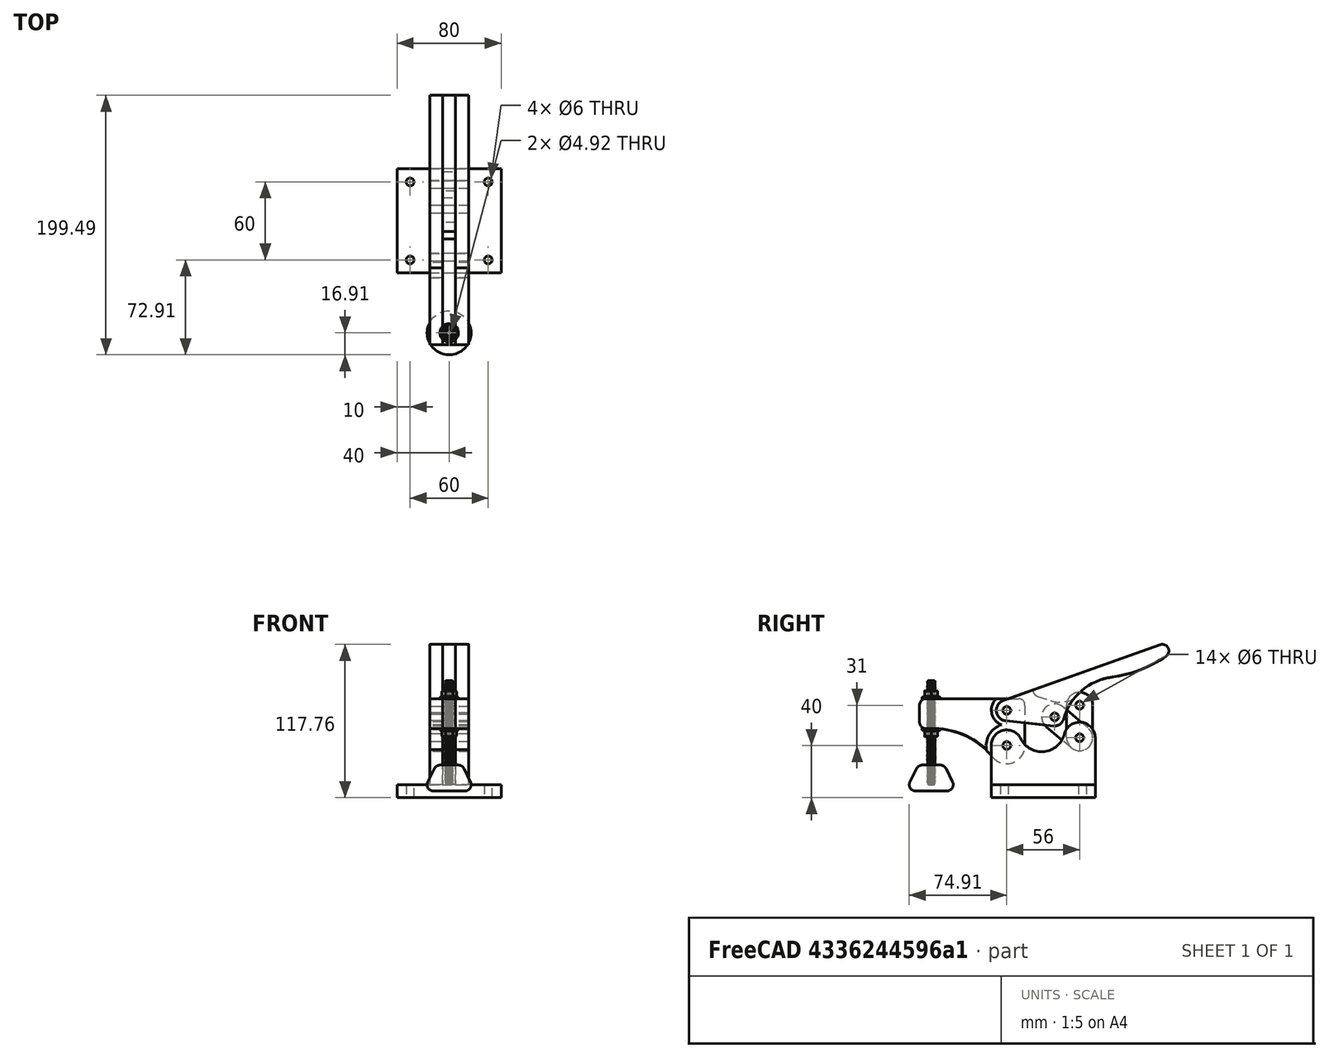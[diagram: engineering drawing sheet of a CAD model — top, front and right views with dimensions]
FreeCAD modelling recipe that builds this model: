
FCSTD DOCUMENT  (FreeCAD 0.19R23756 (Git))
Label: 207 - Tech Draw
License: Creative Commons Attribution-NonCommercial
LicenseURL: http://creativecommons.org/licenses/by-nc/4.0/
objects: TechDraw::DrawViewDimension×57, Part::FeaturePython×14, TechDraw::DrawProjGroupItem×8, TechDraw::DrawViewAnnotation×7, TechDraw::DrawProjGroup×6, Part::Cylinder×4, Part::Compound×4, TechDraw::DrawViewBalloon×4, Part::Cone×1, Part::Fillet×1, TechDraw::DrawSVGTemplate×1, TechDraw::DrawViewImage×1, TechDraw::DrawPage×1
note: 24 computed .brp shape members not serialized (recipe doc carries the construction recipe); baked Part::Feature solids carry a one-line shape summary decoded from their .brp

FEATURE [Part::FeaturePython] b_CLAMP_1_001_  label="CLAMP_1_001"  # a2plus imported part (geometry in sourceFile) (typed FeaturePython)
  a2p_Version = V0.1
  fixedPosition = true
  objectType = a2pPart
  sourceFile = ./CLAMP_1.FCStd
  subassemblyImport = false
  timeLastImport = 1.61442e+09
  updateColors = true
FEATURE [Part::FeaturePython] b_CLAMP_2_001_  label="CLAMP_2_001"  # a2plus imported part (geometry in sourceFile) (typed FeaturePython)
  Placement = pos=(5,-40,10) rot=(0.57735,0.57735,0.57735;2.0944rad)
  a2p_Version = V0.1
  fixedPosition = false
  objectType = a2pPart
  sourceFile = ./CLAMP_2.FCStd
  subassemblyImport = false
  timeLastImport = 1.61442e+09
  updateColors = true
FEATURE [Part::FeaturePython] b_CLAMP_2_001_001  label="CLAMP_2_002"  # a2plus imported part (geometry in sourceFile) (typed FeaturePython)
  Placement = pos=(-15,-40,10) rot=(0.57735,0.57735,0.57735;2.0944rad)
  a2p_Version = V0.1
  fixedPosition = false
  objectType = a2pPart
  sourceFile = ./CLAMP_2.FCStd
  subassemblyImport = false
  timeLastImport = 1.61442e+09
  updateColors = true
FEATURE [Part::Cylinder] Cylinder
  Angle = 360
  AttacherType = Attacher::AttachEngine3D
  Height = 30
  Placement = pos=(15,-28,40) rot=(0,-1,0;1.5708rad)
  Radius = 3
FEATURE [Part::Cylinder] Cylinder001
  Angle = 360
  AttacherType = Attacher::AttachEngine3D
  Height = 30
  Placement = pos=(15,28,46) rot=(0,-1,0;1.5708rad)
  Radius = 3
FEATURE [Part::Compound] Compound
  Links = -> [Cylinder001,Cylinder,b_CLAMP_2_001_001,b_CLAMP_2_001_,b_CLAMP_1_001_]
FEATURE [Part::FeaturePython] b_CLAMP_3_001_  label="CLAMP_3_001"  # a2plus imported part (geometry in sourceFile) (typed FeaturePython)
  Placement = pos=(5,128,8) rot=(0,-1,0;1.5708rad)
  a2p_Version = V0.1
  fixedPosition = false
  objectType = a2pPart
  sourceFile = ./CLAMP_3.FCStd
  subassemblyImport = false
  timeLastImport = 1.61442e+09
  updateColors = true
FEATURE [Part::FeaturePython] b_CLAMP_4_001_  label="CLAMP_4_001"  # a2plus imported part (geometry in sourceFile) (typed FeaturePython)
  Placement = pos=(5,-1e-15,1e-15) rot=(0.57735,0.57735,0.57735;2.0944rad)
  a2p_Version = V0.1
  fixedPosition = false
  objectType = a2pPart
  sourceFile = ./CLAMP_4.FCStd
  subassemblyImport = false
  timeLastImport = 1.61442e+09
  updateColors = true
FEATURE [Part::FeaturePython] b_CLAMP_4_001_001  label="CLAMP_4_002"  # a2plus imported part (geometry in sourceFile) (typed FeaturePython)
  Placement = pos=(-15,-1e-15,1e-15) rot=(0.57735,0.57735,0.57735;2.0944rad)
  a2p_Version = V0.1
  fixedPosition = false
  objectType = a2pPart
  sourceFile = ./CLAMP_4.FCStd
  subassemblyImport = false
  timeLastImport = 1.61442e+09
  updateColors = true
FEATURE [Part::Cylinder] Cylinder002
  Angle = 360
  AttacherType = Attacher::AttachEngine3D
  Height = 30
  Placement = pos=(15,0,3e-15) rot=(0,-1,0;1.5708rad)
  Radius = 3
FEATURE [Part::Cylinder] Cylinder003
  Angle = 360
  AttacherType = Attacher::AttachEngine3D
  Height = 30
  Placement = pos=(15,33,-17) rot=(0,-1,0;1.5708rad)
  Radius = 3
FEATURE [Part::Compound] Compound001
  Links = -> [Cylinder003,Cylinder002,b_CLAMP_4_001_001,b_CLAMP_4_001_,b_CLAMP_3_001_]
  Placement = pos=(0,-28,67) rot=(1,0,0;0.342085rad)
FEATURE [Part::FeaturePython] b_CLAMP_5_001_  label="CLAMP_5_001"  # a2plus imported part (geometry in sourceFile) (typed FeaturePython)
  Placement = pos=(-5,28,46) rot=(0.684791,0.249244,0.684791;2.65306rad)
  a2p_Version = V0.1
  fixedPosition = false
  objectType = a2pPart
  sourceFile = ./CLAMP_5.FCStd
  subassemblyImport = false
  timeLastImport = 1.61442e+09
  updateColors = true
FEATURE [Part::FeaturePython] b_CLAMP_6_001_  label="CLAMP_6_001"  # a2plus imported part (geometry in sourceFile) (typed FeaturePython)
  Placement = pos=(-5,0,-1.1e-15) rot=(0,1,0;1.5708rad)
  a2p_Version = V0.1
  fixedPosition = false
  objectType = a2pPart
  sourceFile = ./CLAMP_6.FCStd
  subassemblyImport = false
  timeLastImport = 1.61442e+09
  updateColors = true
FEATURE [Part::FeaturePython] b_CLAMP_7_001_  label="CLAMP_7_001"  # a2plus imported part (geometry in sourceFile) (typed FeaturePython)
  Placement = pos=(-5,-8,36) rot=(0.57735,-0.57735,-0.57735;2.0944rad)
  a2p_Version = V0.1
  fixedPosition = false
  objectType = a2pPart
  sourceFile = ./CLAMP_7.FCStd
  subassemblyImport = false
  timeLastImport = 1.61442e+09
  updateColors = true
FEATURE [Part::FeaturePython] b_CLAMP_7_001_001  label="CLAMP_7_002"  # a2plus imported part (geometry in sourceFile) (typed FeaturePython)
  Placement = pos=(15,-8,36) rot=(0.57735,-0.57735,-0.57735;2.0944rad)
  a2p_Version = V0.1
  fixedPosition = false
  objectType = a2pPart
  sourceFile = ./CLAMP_7.FCStd
  subassemblyImport = false
  timeLastImport = 1.61442e+09
  updateColors = true
FEATURE [Part::Cone] Cone
  Angle = 360
  AttacherType = Attacher::AttachEngine3D
  Height = 20
  Placement = pos=(0,-58,-35) rot=(0,0,1;0rad)
  Radius1 = 20
  Radius2 = 10
FEATURE [Part::Fillet] Fillet
  Base = -> Cone
  Edges = 2 edges r=5: [Edge1,Edge3]
FEATURE [Part::FeaturePython] ThreadedRod  label="M6x80.0-ThreadedRod"  # Fasteners workbench fastener (typed FeaturePython)
  Placement = pos=(0,-58,-30) rot=(1,0,0;3.14159rad)
  diameter = 8
  invert = false
  length = 80
  matchOuter = false
  offset = 32
  thread = true
FEATURE [Part::FeaturePython] Nut  label="M6-Nut"  # Fasteners workbench fastener (typed FeaturePython)
  Placement = pos=(0,-58,13) rot=(1,0,0;3.14159rad)
  baseObject = -> ThreadedRod [Edge655]
  diameter = 2
  invert = false
  matchOuter = false
  offset = 37
  thread = false
  type = 6
FEATURE [Part::FeaturePython] Clone  label="M6-Nut001"  # Draft clone (typed FeaturePython)
  AttacherType = Attacher::AttachEngine3D
  Fuse = false
  Objects = -> [Nut]
  Placement = pos=(4e-15,-58,36) rot=(0,0,1;3.14159rad)
  Scale = (1,1,1)
FEATURE [Part::Compound] Compound002
  Links = -> [Clone,Nut,ThreadedRod,Fillet,b_CLAMP_7_001_001,b_CLAMP_7_001_,b_CLAMP_6_001_]
  Placement = pos=(0,-28,40) rot=(0,0,1;0rad)
FEATURE [Part::Compound] Compound003
  Links = -> [Compound002,b_CLAMP_5_001_,Compound001,Compound]
FEATURE [TechDraw::DrawSVGTemplate] Template
  EditableTexts = APPROVER_NAME=Bugman; AUTHOR_NAME=Bugman; DATE=2021-03-04; DN=001-21; OWNER_NAME=Bugman; PM=Wood; PN=001-1; REVISION=REV 0; RIGHTS=(R) DO NOT DUPLICATE THIS DRAWING TO THIRD PARTIES WITHOUT OWNER'S PERMISSION !; SCALE=1:1; SHEET=1 of 1; SIZE=A2; TITLELINE-1=Clamp; TITLELINE-2=Detail; TOLERANCE=+/- 1
  Height = 420
  Orientation = 1
  Width = 594
FEATURE [TechDraw::DrawProjGroupItem] ProjItem  label="Front"
  CoarseView = false
  Direction = (1,0,0)
  Focus = 100
  HardHidden = true
  IsoCount = 0
  IsoHidden = true
  IsoVisible = true
  LockPosition = true
  Perspective = false
  Rotation = 0
  RotationVector = (0,1,0)
  ScaleType = 2
  SeamHidden = true
  SeamVisible = true
  SmoothHidden = true
  SmoothVisible = true
  Source = -> [Compound003]
  Type = 0
  X = 0
  XDirection = (0,1,0)
  Y = 0
FEATURE [TechDraw::DrawProjGroupItem] ProjItem001  label="Top"
  CoarseView = false
  Direction = (0,0,1)
  Focus = 100
  HardHidden = true
  IsoCount = 0
  IsoHidden = true
  IsoVisible = true
  LockPosition = true
  Perspective = false
  Rotation = 0
  RotationVector = (1,0,0)
  ScaleType = 2
  SeamHidden = true
  SeamVisible = true
  SmoothHidden = true
  SmoothVisible = true
  Source = -> [Compound003]
  Type = 4
  X = 0
  XDirection = (0,1,0)
  Y = -161.055
FEATURE [TechDraw::DrawProjGroupItem] ProjItem002  label="Left"
  CoarseView = false
  Direction = (1e-16,-1,0)
  Focus = 100
  HardHidden = true
  IsoCount = 0
  IsoHidden = true
  IsoVisible = true
  LockPosition = true
  Perspective = false
  Rotation = 0
  RotationVector = (1,0,0)
  ScaleType = 2
  SeamHidden = true
  SeamVisible = true
  SmoothHidden = true
  SmoothVisible = true
  Source = -> [Compound003]
  Type = 1
  X = 194.685
  XDirection = (1,1e-16,0)
  Y = 0
FEATURE [TechDraw::DrawProjGroup] ProjGroup
  Anchor = -> ProjItem
  AutoDistribute = true
  LockPosition = false
  ProjectionType = 0
  Rotation = 0
  ScaleType = 0
  Source = -> [Compound003]
  Views = -> [ProjItem,ProjItem001,ProjItem002]
  X = 162.918
  Y = 268.672
  spacingX = 15
  spacingY = 15
FEATURE [TechDraw::DrawViewDimension] Dimension001
  Arbitrary = false
  ArbitraryTolerances = false
  EqualTolerance = true
  FormatSpec = %.0f
  FormatSpecTolerance = %+.0f
  Inverted = false
  LockPosition = false
  MeasureType = 1
  OverTolerance = 0
  References2D = -> [ProjItem]
  Rotation = 0
  ScaleType = 0
  TheoreticalExact = false
  Type = 2
  UnderTolerance = 0
  X = -110.673
  Y = -41.733
FEATURE [TechDraw::DrawViewDimension] Dimension002
  Arbitrary = false
  ArbitraryTolerances = false
  EqualTolerance = true
  FormatSpec = %.0f
  FormatSpecTolerance = %+.0f
  Inverted = false
  LockPosition = false
  MeasureType = 1
  OverTolerance = 0
  References2D = -> [ProjItem]
  Rotation = 0
  ScaleType = 0
  TheoreticalExact = false
  Type = 2
  UnderTolerance = 0
  X = -110.959
  Y = -18.111
FEATURE [TechDraw::DrawViewDimension] Dimension003
  Arbitrary = false
  ArbitraryTolerances = false
  EqualTolerance = true
  FormatSpec = %.0f
  FormatSpecTolerance = %+.0f
  Inverted = false
  LockPosition = false
  MeasureType = 1
  OverTolerance = 0
  References2D = -> [ProjItem]
  Rotation = 0
  ScaleType = 0
  TheoreticalExact = false
  Type = 2
  UnderTolerance = 0
  X = -110.968
  Y = 8.22963
FEATURE [TechDraw::DrawViewDimension] Dimension004
  Arbitrary = false
  ArbitraryTolerances = false
  EqualTolerance = true
  FormatSpec = %.0f
  FormatSpecTolerance = %+.0f
  Inverted = false
  LockPosition = false
  MeasureType = 1
  OverTolerance = 0
  References2D = -> [ProjItem]
  Rotation = 0
  ScaleType = 0
  TheoreticalExact = false
  Type = 2
  UnderTolerance = 0
  X = -110.894
  Y = 26.2771
FEATURE [TechDraw::DrawViewDimension] Dimension009
  Arbitrary = false
  ArbitraryTolerances = false
  EqualTolerance = true
  FormatSpec = %.0f
  FormatSpecTolerance = %+.0f
  Inverted = false
  LockPosition = false
  MeasureType = 1
  OverTolerance = 0
  References2D = -> [ProjItem]
  Rotation = 0
  ScaleType = 0
  TheoreticalExact = false
  Type = 1
  UnderTolerance = 0
  X = -86.9639
  Y = 44.832
FEATURE [TechDraw::DrawViewDimension] Dimension013
  Arbitrary = false
  ArbitraryTolerances = false
  EqualTolerance = true
  FormatSpec = %.0f
  FormatSpecTolerance = %+.0f
  Inverted = false
  LockPosition = false
  MeasureType = 1
  OverTolerance = 0
  References2D = -> [ProjItem001]
  Rotation = 0
  ScaleType = 0
  TheoreticalExact = false
  Type = 1
  UnderTolerance = 0
  X = -30.7639
  Y = 51.6646
FEATURE [TechDraw::DrawViewDimension] Dimension014
  Arbitrary = false
  ArbitraryTolerances = false
  EqualTolerance = true
  FormatSpec = %.0f
  FormatSpecTolerance = %+.0f
  Inverted = false
  LockPosition = false
  MeasureType = 1
  OverTolerance = 0
  References2D = -> [ProjItem001]
  Rotation = 0
  ScaleType = 0
  TheoreticalExact = false
  Type = 2
  UnderTolerance = 0
  X = -50.0401
  Y = 36.8654
FEATURE [TechDraw::DrawViewDimension] Dimension015
  Arbitrary = false
  ArbitraryTolerances = false
  EqualTolerance = true
  FormatSpec = ⌀%.0f
  FormatSpecTolerance = %+.0f
  Inverted = false
  LockPosition = false
  MeasureType = 1
  OverTolerance = 0
  References2D = -> [ProjItem001]
  Rotation = 0
  ScaleType = 0
  TheoreticalExact = false
  Type = 5
  UnderTolerance = 0
  X = 18.8755
  Y = -19.5865
FEATURE [TechDraw::DrawViewDimension] Dimension016
  Arbitrary = false
  ArbitraryTolerances = false
  EqualTolerance = true
  FormatSpec = %.0f
  FormatSpecTolerance = %+.0f
  Inverted = false
  LockPosition = false
  MeasureType = 1
  OverTolerance = 0
  References2D = -> [ProjItem001]
  Rotation = 0
  ScaleType = 0
  TheoreticalExact = false
  Type = 1
  UnderTolerance = 0
  X = 2.0466
  Y = 51.5701
FEATURE [TechDraw::DrawViewDimension] Dimension017
  Arbitrary = false
  ArbitraryTolerances = false
  EqualTolerance = true
  FormatSpec = %.0f
  FormatSpecTolerance = %+.0f
  Inverted = false
  LockPosition = false
  MeasureType = 1
  OverTolerance = 0
  References2D = -> [ProjItem001]
  Rotation = 0
  ScaleType = 0
  TheoreticalExact = false
  Type = 2
  UnderTolerance = 0
  X = 107.782
  Y = 2.5895
FEATURE [TechDraw::DrawViewDimension] Dimension018
  Arbitrary = false
  ArbitraryTolerances = false
  EqualTolerance = true
  FormatSpec = %.0f
  FormatSpecTolerance = %+.0f
  Inverted = false
  LockPosition = false
  MeasureType = 1
  OverTolerance = 0
  References2D = -> [ProjItem001]
  Rotation = 0
  ScaleType = 0
  TheoreticalExact = false
  Type = 2
  UnderTolerance = 0
  X = 117.075
  Y = 3.06032
FEATURE [TechDraw::DrawViewDimension] Dimension019
  Arbitrary = false
  ArbitraryTolerances = false
  EqualTolerance = true
  FormatSpec = %.0f
  FormatSpecTolerance = %+.0f
  Inverted = false
  LockPosition = false
  MeasureType = 1
  OverTolerance = 0
  References2D = -> [ProjItem001]
  Rotation = 0
  ScaleType = 0
  TheoreticalExact = false
  Type = 1
  UnderTolerance = 0
  X = -58.9579
  Y = -24.6104
FEATURE [TechDraw::DrawViewDimension] Dimension020
  Arbitrary = false
  ArbitraryTolerances = false
  EqualTolerance = true
  FormatSpec = %.0f
  FormatSpecTolerance = %+.0f
  Inverted = false
  LockPosition = false
  MeasureType = 1
  OverTolerance = 0
  References2D = -> [ProjItem001]
  Rotation = 0
  ScaleType = 0
  TheoreticalExact = false
  Type = 1
  UnderTolerance = 0
  X = -97.8004
  Y = -24.6586
FEATURE [TechDraw::DrawViewDimension] Dimension021
  Arbitrary = false
  ArbitraryTolerances = false
  EqualTolerance = true
  FormatSpec = %.0f
  FormatSpecTolerance = %+.0f
  Inverted = false
  LockPosition = false
  MeasureType = 1
  OverTolerance = 0
  References2D = -> [ProjItem001]
  Rotation = 0
  ScaleType = 0
  TheoreticalExact = false
  Type = 1
  UnderTolerance = 0
  X = -61.9954
  Y = 59.7348
FEATURE [TechDraw::DrawViewDimension] Dimension025
  Arbitrary = false
  ArbitraryTolerances = false
  EqualTolerance = true
  FormatSpec = %.0f
  FormatSpecTolerance = %+.0f
  Inverted = false
  LockPosition = false
  MeasureType = 1
  OverTolerance = 0
  References2D = -> [ProjItem002]
  Rotation = 0
  ScaleType = 0
  TheoreticalExact = false
  Type = 1
  UnderTolerance = 0
  X = 0.189212
  Y = -68.087
FEATURE [TechDraw::DrawViewDimension] Dimension026
  Arbitrary = false
  ArbitraryTolerances = false
  EqualTolerance = true
  FormatSpec = %.0f
  FormatSpecTolerance = %+.0f
  Inverted = false
  LockPosition = false
  MeasureType = 1
  OverTolerance = 0
  References2D = -> [ProjItem002]
  Rotation = 0
  ScaleType = 0
  TheoreticalExact = false
  Type = 1
  UnderTolerance = 0
  X = 23.3865
  Y = -20.3771
FEATURE [TechDraw::DrawViewDimension] Dimension027
  Arbitrary = false
  ArbitraryTolerances = false
  EqualTolerance = true
  FormatSpec = %.0f
  FormatSpecTolerance = %+.0f
  Inverted = false
  LockPosition = false
  MeasureType = 1
  OverTolerance = 0
  References2D = -> [ProjItem002]
  Rotation = 0
  ScaleType = 0
  TheoreticalExact = false
  Type = 1
  UnderTolerance = 0
  X = -1.12997
  Y = 86.0012
FEATURE [TechDraw::DrawViewDimension] Dimension028
  Arbitrary = false
  ArbitraryTolerances = false
  EqualTolerance = true
  FormatSpec = %.0f
  FormatSpecTolerance = %+.0f
  Inverted = false
  LockPosition = false
  MeasureType = 1
  OverTolerance = 0
  References2D = -> [ProjItem002]
  Rotation = 0
  ScaleType = 0
  TheoreticalExact = false
  Type = 1
  UnderTolerance = 0
  X = -0.621813
  Y = 76.2927
FEATURE [TechDraw::DrawViewDimension] Dimension029
  Arbitrary = false
  ArbitraryTolerances = false
  EqualTolerance = true
  FormatSpec = ⌀%.0f
  FormatSpecTolerance = %+.0f
  Inverted = false
  LockPosition = false
  MeasureType = 1
  OverTolerance = 0
  References2D = -> [ProjItem001]
  Rotation = 0
  ScaleType = 0
  TheoreticalExact = false
  Type = 5
  UnderTolerance = 0
  X = -107.896
  Y = 18.3096
FEATURE [TechDraw::DrawViewAnnotation] Annotation
  Font = osifont
  LineSpace = 80
  LockPosition = true
  MaxWidth = -1
  Rotation = 0
  ScaleType = 0
  Text = Front
  TextSize = 8
  TextStyle = 2
  X = 164.991
  Y = 191.348
FEATURE [TechDraw::DrawViewAnnotation] Annotation001
  Font = osifont
  LineSpace = 80
  LockPosition = true
  MaxWidth = -1
  Rotation = 0
  ScaleType = 0
  Text = Top
  TextSize = 8
  TextStyle = 2
  X = 166.458
  Y = 50.0534
FEATURE [TechDraw::DrawViewAnnotation] Annotation002
  Font = osifont
  LineSpace = 80
  LockPosition = true
  MaxWidth = -1
  Rotation = 0
  ScaleType = 0
  Text = Left
  TextSize = 8
  TextStyle = 2
  X = 360.129
  Y = 182.149
FEATURE [TechDraw::DrawViewImage] Image
  Height = 100
  ImageFile = <userpath>/Documentos/BUGMAN-3.png
  LockPosition = true
  Rotation = 0
  Scale = 0.25
  ScaleType = 2
  Width = 100
  X = 516.185
  Y = 32.3781
FEATURE [TechDraw::DrawProjGroupItem] ProjItem003  label="Front001"
  CoarseView = false
  Direction = (1,0,0)
  Focus = 100
  HardHidden = true
  IsoCount = 0
  IsoHidden = true
  IsoVisible = true
  LockPosition = true
  Perspective = false
  Rotation = 0
  RotationVector = (0,1,0)
  ScaleType = 2
  SeamHidden = true
  SeamVisible = true
  SmoothHidden = true
  SmoothVisible = true
  Source = -> [b_CLAMP_4_001_]
  Type = 0
  X = 0
  XDirection = (0,1,0)
  Y = 0
FEATURE [TechDraw::DrawProjGroup] ProjGroup001
  Anchor = -> ProjItem003
  AutoDistribute = true
  LockPosition = false
  ProjectionType = 0
  Rotation = 0
  ScaleType = 0
  Source = -> [b_CLAMP_4_001_]
  Views = -> [ProjItem003]
  X = 495.398
  Y = 359.002
  spacingX = 15
  spacingY = 15
FEATURE [TechDraw::DrawViewDimension] Dimension030
  Arbitrary = false
  ArbitraryTolerances = false
  EqualTolerance = true
  FormatSpec = R%.0f
  FormatSpecTolerance = %+.0f
  Inverted = false
  LockPosition = false
  MeasureType = 1
  OverTolerance = 0
  References2D = -> [ProjItem003]
  Rotation = 0
  ScaleType = 0
  TheoreticalExact = false
  Type = 4
  UnderTolerance = 0
  X = -82.521
  Y = 23.209
FEATURE [TechDraw::DrawViewDimension] Dimension031
  Arbitrary = false
  ArbitraryTolerances = false
  EqualTolerance = true
  FormatSpec = ⌀%.0f
  FormatSpecTolerance = %+.0f
  Inverted = false
  LockPosition = false
  MeasureType = 1
  OverTolerance = 0
  References2D = -> [ProjItem003]
  Rotation = 0
  ScaleType = 0
  TheoreticalExact = false
  Type = 5
  UnderTolerance = 0
  X = -50.7718
  Y = 7.19165
FEATURE [TechDraw::DrawViewDimension] Dimension032
  Arbitrary = false
  ArbitraryTolerances = false
  EqualTolerance = true
  FormatSpec = %.0f
  FormatSpecTolerance = %+.0f
  Inverted = false
  LockPosition = false
  MeasureType = 1
  OverTolerance = 0
  References2D = -> [ProjItem003]
  Rotation = 0
  ScaleType = 0
  TheoreticalExact = false
  Type = 1
  UnderTolerance = 0
  X = -47.3732
  Y = -23.8448
FEATURE [TechDraw::DrawViewDimension] Dimension033
  Arbitrary = false
  ArbitraryTolerances = false
  EqualTolerance = true
  FormatSpec = %.0f
  FormatSpecTolerance = %+.0f
  Inverted = false
  LockPosition = false
  MeasureType = 1
  OverTolerance = 0
  References2D = -> [ProjItem003]
  Rotation = 0
  ScaleType = 0
  TheoreticalExact = false
  Type = 2
  UnderTolerance = 0
  X = -85.2349
  Y = 2.44262
FEATURE [TechDraw::DrawViewDimension] Dimension034
  Arbitrary = false
  ArbitraryTolerances = false
  EqualTolerance = true
  FormatSpec = %.0f
  FormatSpecTolerance = %+.0f
  Inverted = false
  LockPosition = false
  MeasureType = 1
  OverTolerance = 0
  References2D = -> [ProjItem003]
  Rotation = 0
  ScaleType = 0
  TheoreticalExact = false
  Type = 1
  UnderTolerance = 0
  X = 1.10765
  Y = 33.2634
FEATURE [TechDraw::DrawViewDimension] Dimension035
  Arbitrary = false
  ArbitraryTolerances = false
  EqualTolerance = true
  FormatSpec = R%.0f
  FormatSpecTolerance = %+.0f
  Inverted = false
  LockPosition = false
  MeasureType = 1
  OverTolerance = 0
  References2D = -> [ProjItem003]
  Rotation = 0
  ScaleType = 0
  TheoreticalExact = false
  Type = 4
  UnderTolerance = 0
  X = -18.0574
  Y = -20.4452
FEATURE [TechDraw::DrawViewDimension] Dimension036
  Arbitrary = false
  ArbitraryTolerances = false
  EqualTolerance = true
  FormatSpec = R%.0f
  FormatSpecTolerance = %+.0f
  Inverted = false
  LockPosition = false
  MeasureType = 1
  OverTolerance = 0
  References2D = -> [ProjItem003]
  Rotation = 0
  ScaleType = 0
  TheoreticalExact = false
  Type = 4
  UnderTolerance = 0
  X = 77.0053
  Y = 20.8929
FEATURE [TechDraw::DrawViewDimension] Dimension037
  Arbitrary = false
  ArbitraryTolerances = false
  EqualTolerance = true
  FormatSpec = R%.0f
  FormatSpecTolerance = %+.0f
  Inverted = false
  LockPosition = false
  MeasureType = 1
  OverTolerance = 0
  References2D = -> [ProjItem003]
  Rotation = 0
  ScaleType = 0
  TheoreticalExact = false
  Type = 4
  UnderTolerance = 0
  X = 2.537
  Y = -10.2972
FEATURE [TechDraw::DrawViewBalloon] Balloon
  BubbleShape = 0
  EndType = 3
  EndTypeScale = 1
  KinkLength = 10
  LockPosition = false
  OriginX = 34.8817
  OriginY = 37.9256
  Rotation = 0
  ScaleType = 0
  ShapeScale = 1
  SourceView = -> ProjItem
  Text = 1
  TextWrapLen = -1
  X = 54.8817
  Y = 57.9256
FEATURE [TechDraw::DrawViewAnnotation] Annotation003
  Font = osifont
  LineSpace = 80
  LockPosition = true
  MaxWidth = -1
  Rotation = 0
  ScaleType = 0
  Text = Detail - 1
  TextSize = 8
  TextStyle = 2
  X = 499.038
  Y = 294.747
FEATURE [TechDraw::DrawProjGroupItem] ProjItem004  label="Front002"
  CoarseView = false
  Direction = (1,0,0)
  Focus = 100
  HardHidden = true
  IsoCount = 0
  IsoHidden = true
  IsoVisible = true
  LockPosition = true
  Perspective = false
  Rotation = 0
  RotationVector = (0,1,0)
  ScaleType = 2
  SeamHidden = true
  SeamVisible = true
  SmoothHidden = true
  SmoothVisible = true
  Source = -> [b_CLAMP_6_001_]
  Type = 0
  X = 0
  XDirection = (0,1,0)
  Y = 0
FEATURE [TechDraw::DrawProjGroup] ProjGroup002
  Anchor = -> ProjItem004
  AutoDistribute = true
  LockPosition = false
  ProjectionType = 0
  Rotation = 0
  ScaleType = 0
  Source = -> [b_CLAMP_6_001_]
  Views = -> [ProjItem004]
  X = 500.945
  Y = 227.414
  spacingX = 15
  spacingY = 15
FEATURE [TechDraw::DrawViewDimension] Dimension038
  Arbitrary = false
  ArbitraryTolerances = false
  EqualTolerance = true
  FormatSpec = %.0f
  FormatSpecTolerance = %+.0f
  Inverted = false
  LockPosition = false
  MeasureType = 1
  OverTolerance = 0
  References2D = -> [ProjItem004]
  Rotation = 0
  ScaleType = 0
  TheoreticalExact = false
  Type = 2
  UnderTolerance = 0
  X = -54.246
  Y = 15.7665
FEATURE [TechDraw::DrawViewDimension] Dimension039
  Arbitrary = false
  ArbitraryTolerances = false
  EqualTolerance = true
  FormatSpec = %.0f
  FormatSpecTolerance = %+.0f
  Inverted = false
  LockPosition = false
  MeasureType = 1
  OverTolerance = 0
  References2D = -> [ProjItem004]
  Rotation = 0
  ScaleType = 0
  TheoreticalExact = false
  Type = 1
  UnderTolerance = 0
  X = -3.3899
  Y = 40.0569
FEATURE [TechDraw::DrawViewDimension] Dimension040
  Arbitrary = false
  ArbitraryTolerances = false
  EqualTolerance = true
  FormatSpec = %.0f
  FormatSpecTolerance = %+.0f
  Inverted = false
  LockPosition = false
  MeasureType = 1
  OverTolerance = 0
  References2D = -> [ProjItem004]
  Rotation = 0
  ScaleType = 0
  TheoreticalExact = false
  Type = 2
  UnderTolerance = 0
  X = 48.6345
  Y = 5.50858
FEATURE [TechDraw::DrawViewDimension] Dimension041
  Arbitrary = false
  ArbitraryTolerances = false
  EqualTolerance = true
  FormatSpec = %.0f
  FormatSpecTolerance = %+.0f
  Inverted = false
  LockPosition = false
  MeasureType = 1
  OverTolerance = 0
  References2D = -> [ProjItem004]
  Rotation = 0
  ScaleType = 0
  TheoreticalExact = false
  Type = 2
  UnderTolerance = 0
  X = 48.6217
  Y = 23.2937
FEATURE [TechDraw::DrawViewDimension] Dimension042
  Arbitrary = false
  ArbitraryTolerances = false
  EqualTolerance = true
  FormatSpec = R%.0f
  FormatSpecTolerance = %+.0f
  Inverted = false
  LockPosition = false
  MeasureType = 1
  OverTolerance = 0
  References2D = -> [ProjItem004]
  Rotation = 0
  ScaleType = 0
  TheoreticalExact = false
  Type = 4
  UnderTolerance = 0
  X = 38.8966
  Y = -28.5815
FEATURE [TechDraw::DrawViewDimension] Dimension043
  Arbitrary = false
  ArbitraryTolerances = false
  EqualTolerance = true
  FormatSpec = R%.0f
  FormatSpecTolerance = %+.0f
  Inverted = false
  LockPosition = false
  MeasureType = 1
  OverTolerance = 0
  References2D = -> [ProjItem004]
  Rotation = 0
  ScaleType = 0
  TheoreticalExact = false
  Type = 4
  UnderTolerance = 0
  X = -17.6217
  Y = -16.3323
FEATURE [TechDraw::DrawViewDimension] Dimension044
  Arbitrary = false
  ArbitraryTolerances = false
  EqualTolerance = true
  FormatSpec = R%.0f
  FormatSpecTolerance = %+.0f
  Inverted = false
  LockPosition = false
  MeasureType = 1
  OverTolerance = 0
  References2D = -> [ProjItem004]
  Rotation = 0
  ScaleType = 0
  TheoreticalExact = false
  Type = 4
  UnderTolerance = 0
  X = -49.4266
  Y = -2.36388
FEATURE [TechDraw::DrawViewDimension] Dimension045
  Arbitrary = false
  ArbitraryTolerances = false
  EqualTolerance = true
  FormatSpec = %.0f
  FormatSpecTolerance = %+.0f
  Inverted = false
  LockPosition = false
  MeasureType = 1
  OverTolerance = 0
  References2D = -> [ProjItem004]
  Rotation = 0
  ScaleType = 0
  TheoreticalExact = false
  Type = 1
  UnderTolerance = 0
  X = 32.2106
  Y = 6.97426
FEATURE [TechDraw::DrawViewBalloon] Balloon001
  BubbleShape = 0
  EndType = 3
  EndTypeScale = 1
  KinkLength = 10
  LockPosition = false
  OriginX = -64.47
  OriginY = 17.29
  Rotation = 0
  ScaleType = 0
  ShapeScale = 1
  SourceView = -> ProjItem
  Text = 2
  TextWrapLen = -1
  X = -43.9566
  Y = 30.7213
FEATURE [TechDraw::DrawViewAnnotation] Annotation004
  Font = osifont
  LineSpace = 80
  LockPosition = false
  MaxWidth = -1
  Rotation = 0
  ScaleType = 0
  Text = Detail - 2
  TextSize = 8
  TextStyle = 2
  X = 501.435
  Y = 166.067
FEATURE [TechDraw::DrawViewDimension] Dimension046
  Arbitrary = false
  ArbitraryTolerances = false
  EqualTolerance = true
  FormatSpec = ⌀%.0f
  FormatSpecTolerance = %+.0f
  Inverted = false
  LockPosition = false
  MeasureType = 1
  OverTolerance = 0
  References2D = -> [ProjItem004]
  Rotation = 0
  ScaleType = 0
  TheoreticalExact = false
  Type = 5
  UnderTolerance = 0
  X = 15.0662
  Y = 13.6537
FEATURE [Part::FeaturePython] b_CLAMP_5_001_001  label="CLAMP_5_002"  # a2plus imported part (geometry in sourceFile) (typed FeaturePython)
  Placement = pos=(-5,28,46) rot=(0.57735,0.57735,0.57735;2.0944rad)
  a2p_Version = V0.1
  fixedPosition = false
  objectType = a2pPart
  sourceFile = ./CLAMP_5.FCStd
  subassemblyImport = false
  timeLastImport = 1.61442e+09
  updateColors = true
FEATURE [TechDraw::DrawProjGroupItem] ProjItem005  label="Front003"
  CoarseView = false
  Direction = (1,0,0)
  Focus = 100
  HardHidden = true
  IsoCount = 0
  IsoHidden = true
  IsoVisible = true
  LockPosition = true
  Perspective = false
  Rotation = 0
  RotationVector = (0,1,0)
  ScaleType = 2
  SeamHidden = true
  SeamVisible = true
  SmoothHidden = true
  SmoothVisible = true
  Source = -> [b_CLAMP_5_001_001]
  Type = 0
  X = 0
  XDirection = (0,1,0)
  Y = 0
FEATURE [TechDraw::DrawProjGroup] ProjGroup003
  Anchor = -> ProjItem005
  AutoDistribute = true
  LockPosition = false
  ProjectionType = 0
  Rotation = 0
  ScaleType = 0
  Source = -> [b_CLAMP_5_001_001]
  Views = -> [ProjItem005]
  X = 329.054
  Y = 91.0644
  spacingX = 15
  spacingY = 15
FEATURE [TechDraw::DrawViewDimension] Dimension047
  Arbitrary = false
  ArbitraryTolerances = false
  EqualTolerance = true
  FormatSpec = %.0f
  FormatSpecTolerance = %+.0f
  Inverted = false
  LockPosition = false
  MeasureType = 1
  OverTolerance = 0
  References2D = -> [ProjItem005]
  Rotation = 0
  ScaleType = 0
  TheoreticalExact = false
  Type = 1
  UnderTolerance = 0
  X = -1.23782
  Y = 37.5658
FEATURE [TechDraw::DrawViewDimension] Dimension048
  Arbitrary = false
  ArbitraryTolerances = false
  EqualTolerance = true
  FormatSpec = %.0f
  FormatSpecTolerance = %+.0f
  Inverted = false
  LockPosition = false
  MeasureType = 1
  OverTolerance = 0
  References2D = -> [ProjItem005]
  Rotation = 0
  ScaleType = 0
  TheoreticalExact = false
  Type = 2
  UnderTolerance = 0
  X = 16.2679
  Y = 2.50715
FEATURE [TechDraw::DrawViewDimension] Dimension049
  Arbitrary = false
  ArbitraryTolerances = false
  EqualTolerance = true
  FormatSpec = ⌀%.0f
  FormatSpecTolerance = %+.0f
  Inverted = false
  LockPosition = false
  MeasureType = 1
  OverTolerance = 0
  References2D = -> [ProjItem005]
  Rotation = 0
  ScaleType = 0
  TheoreticalExact = false
  Type = 5
  UnderTolerance = 0
  X = -7.34236
  Y = 9.13318
FEATURE [TechDraw::DrawViewBalloon] Balloon002
  BubbleShape = 0
  EndType = 3
  EndTypeScale = 1
  KinkLength = 10
  LockPosition = false
  OriginX = 29.0463
  OriginY = 1.36107
  Rotation = 0
  ScaleType = 0
  ShapeScale = 1
  SourceView = -> ProjItem
  Text = 3
  TextWrapLen = -1
  X = 57.521
  Y = 14.0634
FEATURE [TechDraw::DrawViewAnnotation] Annotation005
  Font = osifont
  LineSpace = 80
  LockPosition = true
  MaxWidth = -1
  Rotation = 0
  ScaleType = 0
  Text = Detail - 3
  TextSize = 8
  TextStyle = 2
  X = 330.421
  Y = 42.2761
FEATURE [TechDraw::DrawViewDimension] Dimension051
  Arbitrary = false
  ArbitraryTolerances = false
  EqualTolerance = true
  FormatSpec = R%.0f
  FormatSpecTolerance = %+.0f
  Inverted = false
  LockPosition = false
  MeasureType = 1
  OverTolerance = 0
  References2D = -> [ProjItem]
  Rotation = 0
  ScaleType = 0
  TheoreticalExact = false
  Type = 4
  UnderTolerance = 0
  X = -48.739
  Y = 12.8939
FEATURE [TechDraw::DrawViewDimension] Dimension052
  Arbitrary = false
  ArbitraryTolerances = false
  EqualTolerance = true
  FormatSpec = R%.0f
  FormatSpecTolerance = %+.0f
  Inverted = false
  LockPosition = false
  MeasureType = 1
  OverTolerance = 0
  References2D = -> [ProjItem]
  Rotation = 0
  ScaleType = 0
  TheoreticalExact = false
  Type = 4
  UnderTolerance = 0
  X = -45.9023
  Y = 0.257878
FEATURE [TechDraw::DrawProjGroupItem] ProjItem006  label="Front004"
  CoarseView = false
  Direction = (1,0,0)
  Focus = 100
  HardHidden = true
  IsoCount = 0
  IsoHidden = true
  IsoVisible = true
  LockPosition = true
  Perspective = false
  Rotation = 0
  RotationVector = (0,1,0)
  ScaleType = 2
  SeamHidden = true
  SeamVisible = true
  SmoothHidden = true
  SmoothVisible = true
  Source = -> [b_CLAMP_2_001_001]
  Type = 0
  X = 0
  XDirection = (0,1,0)
  Y = 0
FEATURE [TechDraw::DrawProjGroup] ProjGroup004
  Anchor = -> ProjItem006
  AutoDistribute = true
  LockPosition = false
  ProjectionType = 0
  Rotation = 0
  ScaleType = 0
  Source = -> [b_CLAMP_2_001_001]
  Views = -> [ProjItem006]
  X = 150.118
  Y = 365.55
  spacingX = 15
  spacingY = 15
FEATURE [TechDraw::DrawViewDimension] Dimension053
  Arbitrary = false
  ArbitraryTolerances = false
  EqualTolerance = true
  FormatSpec = R%.0f
  FormatSpecTolerance = %+.0f
  Inverted = false
  LockPosition = false
  MeasureType = 1
  OverTolerance = 0
  References2D = -> [ProjItem006]
  Rotation = 0
  ScaleType = 0
  TheoreticalExact = false
  Type = 4
  UnderTolerance = 0
  X = -7.06228
  Y = 15.537
FEATURE [TechDraw::DrawViewDimension] Dimension054
  Arbitrary = false
  ArbitraryTolerances = false
  EqualTolerance = true
  FormatSpec = R%.0f
  FormatSpecTolerance = %+.0f
  Inverted = false
  LockPosition = false
  MeasureType = 1
  OverTolerance = 0
  References2D = -> [ProjItem006]
  Rotation = 0
  ScaleType = 0
  TheoreticalExact = false
  Type = 4
  UnderTolerance = 0
  X = -21.4223
  Y = 28.4845
FEATURE [TechDraw::DrawViewDimension] Dimension055
  Arbitrary = false
  ArbitraryTolerances = false
  EqualTolerance = true
  FormatSpec = R%.0f
  FormatSpecTolerance = %+.0f
  Inverted = false
  LockPosition = false
  MeasureType = 1
  OverTolerance = 0
  References2D = -> [ProjItem006]
  Rotation = 0
  ScaleType = 0
  TheoreticalExact = false
  Type = 4
  UnderTolerance = 0
  X = 35.076
  Y = 37.1947
FEATURE [TechDraw::DrawViewDimension] Dimension056
  Arbitrary = false
  ArbitraryTolerances = false
  EqualTolerance = true
  FormatSpec = ⌀%.0f
  FormatSpecTolerance = %+.0f
  Inverted = false
  LockPosition = false
  MeasureType = 1
  OverTolerance = 0
  References2D = -> [ProjItem006]
  Rotation = 0
  ScaleType = 0
  TheoreticalExact = false
  Type = 5
  UnderTolerance = 0
  X = 17.8911
  Y = 7.5331
FEATURE [TechDraw::DrawViewDimension] Dimension057
  Arbitrary = false
  ArbitraryTolerances = false
  EqualTolerance = true
  FormatSpec = %.0f
  FormatSpecTolerance = %+.0f
  Inverted = false
  LockPosition = false
  MeasureType = 1
  OverTolerance = 0
  References2D = -> [ProjItem006]
  Rotation = 0
  ScaleType = 0
  TheoreticalExact = false
  Type = 1
  UnderTolerance = 0
  X = -0.706228
  Y = -28.2374
FEATURE [TechDraw::DrawViewDimension] Dimension058
  Arbitrary = false
  ArbitraryTolerances = false
  EqualTolerance = true
  FormatSpec = %.0f
  FormatSpecTolerance = %+.0f
  Inverted = false
  LockPosition = false
  MeasureType = 1
  OverTolerance = 0
  References2D = -> [ProjItem006]
  Rotation = 0
  ScaleType = 0
  TheoreticalExact = false
  Type = 2
  UnderTolerance = 0
  X = -52.7121
  Y = -6.6459
FEATURE [TechDraw::DrawViewDimension] Dimension059
  Arbitrary = false
  ArbitraryTolerances = false
  EqualTolerance = true
  FormatSpec = %.0f
  FormatSpecTolerance = %+.0f
  Inverted = false
  LockPosition = false
  MeasureType = 1
  OverTolerance = 0
  References2D = -> [ProjItem006]
  Rotation = 0
  ScaleType = 0
  TheoreticalExact = false
  Type = 2
  UnderTolerance = 0
  X = 47.5331
  Y = -4.58754
FEATURE [TechDraw::DrawViewDimension] Dimension060
  Arbitrary = false
  ArbitraryTolerances = false
  EqualTolerance = true
  FormatSpec = %.0f
  FormatSpecTolerance = %+.0f
  Inverted = false
  LockPosition = false
  MeasureType = 1
  OverTolerance = 0
  References2D = -> [ProjItem006]
  Rotation = 0
  ScaleType = 0
  TheoreticalExact = false
  Type = 2
  UnderTolerance = 0
  X = -62.9247
  Y = -0.238708
FEATURE [TechDraw::DrawViewDimension] Dimension061
  Arbitrary = false
  ArbitraryTolerances = false
  EqualTolerance = true
  FormatSpec = %.0f
  FormatSpecTolerance = %+.0f
  Inverted = false
  LockPosition = false
  MeasureType = 1
  OverTolerance = 0
  References2D = -> [ProjItem006]
  Rotation = 0
  ScaleType = 0
  TheoreticalExact = false
  Type = 1
  UnderTolerance = 0
  X = -21.728
  Y = 38.0668
FEATURE [TechDraw::DrawViewBalloon] Balloon003
  BubbleShape = 0
  EndType = 3
  EndTypeScale = 1
  KinkLength = 10
  LockPosition = false
  OriginX = 44
  OriginY = -27
  Rotation = 0
  ScaleType = 0
  ShapeScale = 1
  SourceView = -> ProjItem
  Text = 4
  TextWrapLen = -1
  X = 78.3058
  Y = -2.27336
  expr: OriginY = -27
FEATURE [TechDraw::DrawViewAnnotation] Annotation006
  Font = osifont
  LineSpace = 80
  LockPosition = false
  MaxWidth = -1
  Rotation = 0
  ScaleType = 0
  Text = Detail - 4
  TextSize = 8
  TextStyle = 2
  X = 157.746
  Y = 322.146
FEATURE [TechDraw::DrawProjGroupItem] ProjItem007  label="Front005"
  CoarseView = false
  Direction = (0.577,-0.577,0.577)
  Focus = 100
  HardHidden = true
  IsoCount = 0
  IsoHidden = true
  IsoVisible = true
  LockPosition = true
  Perspective = false
  Rotation = 0
  RotationVector = (0.707,0.707,0)
  Scale = 0.5
  ScaleType = 2
  SeamHidden = true
  SeamVisible = true
  SmoothHidden = true
  SmoothVisible = true
  Source = -> [Compound003]
  Type = 0
  X = 0
  XDirection = (0.707,0.707,0)
  Y = 0
FEATURE [TechDraw::DrawProjGroup] ProjGroup005
  Anchor = -> ProjItem007
  AutoDistribute = true
  LockPosition = false
  ProjectionType = 0
  Rotation = 0
  Scale = 0.5
  ScaleType = 2
  Source = -> [Compound003]
  Views = -> [ProjItem007]
  X = 426.363
  Y = 103.737
  spacingX = 15
  spacingY = 15
FEATURE [TechDraw::DrawViewDimension] Dimension062
  Arbitrary = false
  ArbitraryTolerances = false
  EqualTolerance = true
  FormatSpec = %.0f
  FormatSpecTolerance = %+.0f
  Inverted = false
  LockPosition = false
  MeasureType = 1
  OverTolerance = 0
  References2D = -> [ProjItem001]
  Rotation = 0
  ScaleType = 0
  TheoreticalExact = false
  Type = 1
  UnderTolerance = 0
  X = 3.86303
  Y = 59.8858
FEATURE [TechDraw::DrawViewDimension] Dimension
  Arbitrary = false
  ArbitraryTolerances = false
  EqualTolerance = true
  FormatSpec = %.0f
  FormatSpecTolerance = %+.0f
  Inverted = false
  LockPosition = false
  MeasureType = 1
  OverTolerance = 0
  References2D = -> [ProjItem]
  Rotation = 0
  ScaleType = 0
  TheoreticalExact = false
  Type = 2
  UnderTolerance = 0
  X = -110.79
  Y = -63.4731
FEATURE [TechDraw::DrawViewDimension] Dimension063
  Arbitrary = false
  ArbitraryTolerances = false
  EqualTolerance = true
  FormatSpec = %.0f
  FormatSpecTolerance = %+.0f
  Inverted = false
  LockPosition = false
  MeasureType = 1
  OverTolerance = 0
  References2D = -> [ProjItem]
  Rotation = 0
  ScaleType = 0
  TheoreticalExact = false
  Type = 2
  UnderTolerance = 0
  X = -121.949
  Y = -12.8031
FEATURE [TechDraw::DrawViewDimension] Dimension064
  Arbitrary = false
  ArbitraryTolerances = false
  EqualTolerance = true
  FormatSpec = %.0f
  FormatSpecTolerance = %+.0f
  Inverted = false
  LockPosition = false
  MeasureType = 1
  OverTolerance = 0
  References2D = -> [ProjItem]
  Rotation = 0
  ScaleType = 0
  TheoreticalExact = false
  Type = 6
  UnderTolerance = 0
  X = 11.65
  Y = -25.9573
FEATURE [TechDraw::DrawViewDimension] Dimension065
  Arbitrary = false
  ArbitraryTolerances = false
  EqualTolerance = true
  FormatSpec = %.0f
  FormatSpecTolerance = %+.0f
  Inverted = false
  LockPosition = false
  MeasureType = 1
  OverTolerance = 0
  References2D = -> [ProjItem]
  Rotation = 0
  ScaleType = 0
  TheoreticalExact = false
  Type = 2
  UnderTolerance = 0
  X = 49.4072
  Y = -51.6343
FEATURE [TechDraw::DrawViewDimension] Dimension066
  Arbitrary = false
  ArbitraryTolerances = false
  EqualTolerance = true
  FormatSpec = %.0f
  FormatSpecTolerance = %+.0f
  Inverted = false
  LockPosition = false
  MeasureType = 1
  OverTolerance = 0
  References2D = -> [ProjItem]
  Rotation = 0
  ScaleType = 0
  TheoreticalExact = false
  Type = 2
  UnderTolerance = 0
  X = 49.4072
  Y = -28.1848
FEATURE [TechDraw::DrawViewDimension] Dimension067
  Arbitrary = false
  ArbitraryTolerances = false
  EqualTolerance = true
  FormatSpec = R%.0f
  FormatSpecTolerance = %+.0f
  Inverted = false
  LockPosition = false
  MeasureType = 1
  OverTolerance = 0
  References2D = -> [ProjItem]
  Rotation = 0
  ScaleType = 0
  TheoreticalExact = false
  Type = 4
  UnderTolerance = 0
  X = -57.2014
  Y = -50.8194
FEATURE [TechDraw::DrawPage] Page
  KeepUpdated = true
  NextBalloonIndex = 6
  ProjectionType = 0
  Template = -> Template
  Views = -> [ProjGroup,Dimension001,Dimension002,Dimension003,Dimension004,Dimension009,Dimension013,Dimension014,Dimension015,Dimension016,Dimension017,Dimension018,Dimension019,Dimension020,Dimension021,Dimension025,Dimension026,Dimension027,Dimension028,Dimension029,Annotation,Annotation001,Annotation002,Image,ProjGroup001,Dimension030,Dimension031,Dimension032,Dimension033,Dimension034,Dimension035,+44 more]
